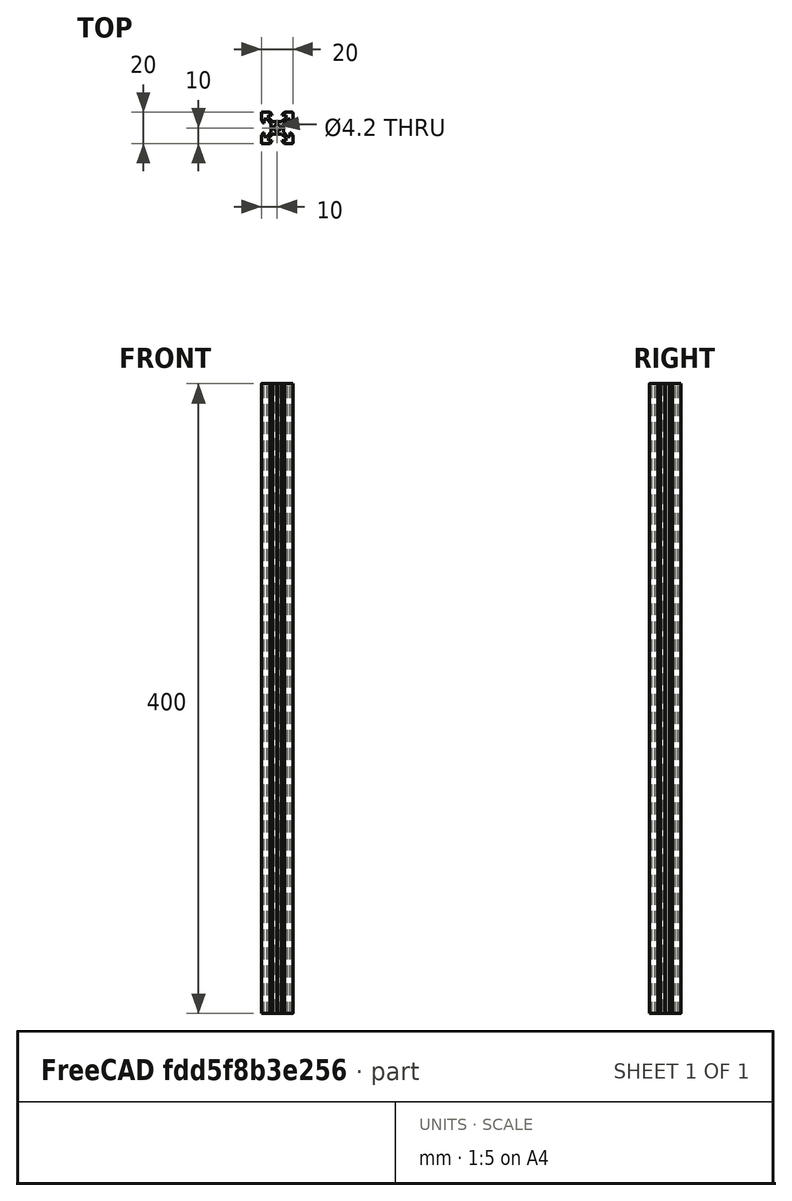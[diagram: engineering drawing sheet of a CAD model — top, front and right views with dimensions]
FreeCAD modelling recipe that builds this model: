
FCSTD DOCUMENT  (FreeCAD 0.19R)
Label: 2020-400
License: All rights reserved
LicenseURL: http://en.wikipedia.org/wiki/All_rights_reserved
objects: Sketcher::SketchObject×1, PartDesign::Pad×1, PartDesign::Body×1
note: 4 computed .brp shape members not serialized (recipe doc carries the construction recipe); baked Part::Feature solids carry a one-line shape summary decoded from their .brp

FEATURE [Sketcher::SketchObject] Sketch
  FullyConstrained = true
  MapMode = 5
  Support = -> [XY_Plane]
  sketch-geometry (65):
    g0: LineSegment StartX=-10 StartY=4.58 StartZ=0 EndX=-10 EndY=9.5 EndZ=0
    g1: LineSegment StartX=-9.5 StartY=10 StartZ=0 EndX=-4.58 EndY=10 EndZ=0
    g2: LineSegment StartX=-5.5 StartY=8.2 StartZ=0 EndX=-3.125 EndY=8.2 EndZ=0
    g3: LineSegment StartX=-8.2 StartY=5.5 StartZ=0 EndX=-8.2 EndY=3.125 EndZ=0
    g4: LineSegment StartX=-0.125 StartY=3.9 StartZ=0 EndX=-2.83934 EndY=3.9 EndZ=0
    g5: LineSegment StartX=-3.9 StartY=2.83934 StartZ=0 EndX=-3.9 EndY=0.125 EndZ=0
    g6: ArcOfCircle CenterX=0 CenterY=3.9 CenterZ=0 NormalX=0 NormalY=0 NormalZ=1 AngleXU=0 Radius=0.125 StartAngle=3.14159 EndAngle=6.28319
    g7: ArcOfCircle CenterX=-3.9 CenterY=0 CenterZ=0 NormalX=0 NormalY=0 NormalZ=1 AngleXU=0 Radius=0.125 StartAngle=4.71239 EndAngle=7.85398
    g8: ArcOfCircle CenterX=-9.5 CenterY=9.5 CenterZ=0 NormalX=0 NormalY=0 NormalZ=1 AngleXU=0 Radius=0.5 StartAngle=1.5708 EndAngle=3.14159
    g9: LineSegment StartX=-5.5 StartY=8.2 StartZ=0 EndX=-5.5 EndY=6.56066 EndZ=0
    g10: LineSegment StartX=-8.2 StartY=5.5 StartZ=0 EndX=-6.56066 EndY=5.5 EndZ=0
    g11: LineSegment StartX=-4.58 StartY=10 StartZ=0 EndX=-3.125 EndY=8.545 EndZ=0
    g12: LineSegment StartX=-3.125 StartY=8.545 StartZ=0 EndX=-3.125 EndY=8.2 EndZ=0
    g13: LineSegment StartX=-10 StartY=4.58 StartZ=0 EndX=-8.545 EndY=3.125 EndZ=0
    g14: LineSegment StartX=-8.545 StartY=3.125 StartZ=0 EndX=-8.2 EndY=3.125 EndZ=0
    g15: LineSegment StartX=-5.5 StartY=6.56066 StartZ=0 EndX=-2.83934 EndY=3.9 EndZ=0
    g16: LineSegment StartX=-6.56066 StartY=5.5 StartZ=0 EndX=-3.9 EndY=2.83934 EndZ=0
    g17: Circle CenterX=0 CenterY=0 CenterZ=0 NormalX=0 NormalY=0 NormalZ=1 AngleXU=0 Radius=2.1
    g18: LineSegment StartX=0.125 StartY=3.9 StartZ=0 EndX=2.83934 EndY=3.9 EndZ=0
    g19: LineSegment StartX=2.83934 StartY=3.9 StartZ=0 EndX=5.5 EndY=6.56066 EndZ=0
    g20: LineSegment StartX=5.5 StartY=6.56066 StartZ=0 EndX=5.5 EndY=8.2 EndZ=0
    g21: LineSegment StartX=3.125 StartY=8.2 StartZ=0 EndX=3.125 EndY=8.545 EndZ=0
    g22: LineSegment StartX=5.5 StartY=8.2 StartZ=0 EndX=3.125 EndY=8.2 EndZ=0
    g23: LineSegment StartX=4.58 StartY=10 StartZ=0 EndX=9.5 EndY=10 EndZ=0
    g24: ArcOfCircle CenterX=9.5 CenterY=9.5 CenterZ=0 NormalX=0 NormalY=0 NormalZ=1 AngleXU=0 Radius=0.5 StartAngle=1.9e-15 EndAngle=1.5708
    g25: LineSegment StartX=10 StartY=9.5 StartZ=0 EndX=10 EndY=4.58 EndZ=0
    g26: LineSegment StartX=10 StartY=4.58 StartZ=0 EndX=8.545 EndY=3.125 EndZ=0
    g27: LineSegment StartX=8.545 StartY=3.125 StartZ=0 EndX=8.2 EndY=3.125 EndZ=0
    g28: LineSegment StartX=8.2 StartY=3.125 StartZ=0 EndX=8.2 EndY=5.5 EndZ=0
    g29: LineSegment StartX=8.2 StartY=5.5 StartZ=0 EndX=6.56066 EndY=5.5 EndZ=0
    g30: LineSegment StartX=6.56066 StartY=5.5 StartZ=0 EndX=3.9 EndY=2.83934 EndZ=0
    g31: LineSegment StartX=3.9 StartY=2.83934 StartZ=0 EndX=3.9 EndY=0.125 EndZ=0
    g32: ArcOfCircle CenterX=3.9 CenterY=0 CenterZ=0 NormalX=0 NormalY=0 NormalZ=1 AngleXU=0 Radius=0.125 StartAngle=1.5708 EndAngle=4.71239
    g33: LineSegment StartX=3.9 StartY=-0.125 StartZ=0 EndX=3.9 EndY=-2.83934 EndZ=0
    g34: LineSegment StartX=3.9 StartY=-2.83934 StartZ=0 EndX=6.56066 EndY=-5.5 EndZ=0
    g35: LineSegment StartX=6.56066 StartY=-5.5 StartZ=0 EndX=8.2 EndY=-5.5 EndZ=0
    g36: LineSegment StartX=8.2 StartY=-5.5 StartZ=0 EndX=8.2 EndY=-3.125 EndZ=0
    g37: LineSegment StartX=8.2 StartY=-3.125 StartZ=0 EndX=8.545 EndY=-3.125 EndZ=0
    g38: LineSegment StartX=8.545 StartY=-3.125 StartZ=0 EndX=10 EndY=-4.58 EndZ=0
    g39: LineSegment StartX=10 StartY=-4.58 StartZ=0 EndX=10 EndY=-9.5 EndZ=0
    g40: ArcOfCircle CenterX=9.5 CenterY=-9.5 CenterZ=0 NormalX=0 NormalY=0 NormalZ=1 AngleXU=0 Radius=0.5 StartAngle=4.71239 EndAngle=6.28319
    g41: LineSegment StartX=9.5 StartY=-10 StartZ=0 EndX=4.58 EndY=-10 EndZ=0
    g42: LineSegment StartX=4.58 StartY=-10 StartZ=0 EndX=3.125 EndY=-8.545 EndZ=0
    g43: LineSegment StartX=2.83934 StartY=-3.9 StartZ=0 EndX=5.5 EndY=-6.56066 EndZ=0
    g44: LineSegment StartX=3.125 StartY=-8.545 StartZ=0 EndX=3.125 EndY=-8.2 EndZ=0
    g45: LineSegment StartX=3.125 StartY=-8.2 StartZ=0 EndX=5.5 EndY=-8.2 EndZ=0
    g46: LineSegment StartX=5.5 StartY=-8.2 StartZ=0 EndX=5.5 EndY=-6.56066 EndZ=0
    g47: ArcOfCircle CenterX=0 CenterY=-3.9 CenterZ=0 NormalX=0 NormalY=0 NormalZ=1 AngleXU=0 Radius=0.125 StartAngle=0 EndAngle=3.14159
    g48: LineSegment StartX=0.125 StartY=-3.9 StartZ=0 EndX=2.83934 EndY=-3.9 EndZ=0
    g49: LineSegment StartX=-0.125 StartY=-3.9 StartZ=0 EndX=-2.83934 EndY=-3.9 EndZ=0
    g50: LineSegment StartX=-3.9 StartY=-0.125 StartZ=0 EndX=-3.9 EndY=-2.83934 EndZ=0
    g51: LineSegment StartX=-3.9 StartY=-2.83934 StartZ=0 EndX=-6.56066 EndY=-5.5 EndZ=0
    g52: LineSegment StartX=-6.56066 StartY=-5.5 StartZ=0 EndX=-8.2 EndY=-5.5 EndZ=0
    g53: LineSegment StartX=-8.2 StartY=-5.5 StartZ=0 EndX=-8.2 EndY=-3.125 EndZ=0
    g54: LineSegment StartX=-8.2 StartY=-3.125 StartZ=0 EndX=-8.545 EndY=-3.125 EndZ=0
    g55: LineSegment StartX=-8.545 StartY=-3.125 StartZ=0 EndX=-10 EndY=-4.58 EndZ=0
    g56: LineSegment StartX=-10 StartY=-4.58 StartZ=0 EndX=-10 EndY=-9.5 EndZ=0
    g57: ArcOfCircle CenterX=-9.5 CenterY=-9.5 CenterZ=0 NormalX=0 NormalY=0 NormalZ=1 AngleXU=0 Radius=0.5 StartAngle=3.14159 EndAngle=4.71239
    g58: LineSegment StartX=-9.5 StartY=-10 StartZ=0 EndX=-4.58 EndY=-10 EndZ=0
    g59: LineSegment StartX=-4.58 StartY=-10 StartZ=0 EndX=-3.125 EndY=-8.545 EndZ=0
    g60: LineSegment StartX=-2.83934 StartY=-3.9 StartZ=0 EndX=-5.5 EndY=-6.56066 EndZ=0
    g61: LineSegment StartX=-5.5 StartY=-6.56066 StartZ=0 EndX=-5.5 EndY=-8.2 EndZ=0
    g62: LineSegment StartX=-5.5 StartY=-8.2 StartZ=0 EndX=-3.125 EndY=-8.2 EndZ=0
    g63: LineSegment StartX=-3.125 StartY=-8.545 StartZ=0 EndX=-3.125 EndY=-8.2 EndZ=0
    g64: LineSegment StartX=3.125 StartY=8.545 StartZ=0 EndX=4.58 EndY=10 EndZ=0
  constraints (194):
    c: Diameter(g17) = 4.2
    c: Radius(g32) = 0.125
    c: Coincident(g-1,g17)
    c: DistanceY(g57,g1) = 20
    c: DistanceX(g56,g39) = 20
    c: Radius(g57) = 0.5
    c: DistanceX(g56,g17) = 10
    c: DistanceY(g57,g17) = 10
    c: Distance(g5,g4) = 1.5
    c: DistanceY(g20,g23) = 1.8
    c: DistanceY(g18,g20) = 4.3
    c: DistanceX(g11,g21) = 6.25
    c: DistanceX(g1,g23) = 9.16
    c: DistanceX(g2,g20) = 11
    c: Coincident(g6,g18)
    c: Coincident(g6,g4)
    c: Coincident(g4,g15)
    c: Coincident(g18,g19)
    c: Coincident(g5,g16)
    c: Coincident(g16,g10)
    c: Coincident(g15,g9)
    c: Coincident(g12,g2)
    c: Coincident(g2,g9)
    c: Coincident(g12,g11)
    c: Coincident(g1,g11)
    c: Coincident(g23,g64)
    c: Coincident(g22,g21)
    c: Coincident(g64,g21)
    c: Coincident(g22,g20)
    c: Coincident(g19,g20)
    c: Coincident(g25,g26)
    c: Coincident(g27,g26)
    c: Coincident(g27,g28)
    c: Coincident(g28,g29)
    c: Coincident(g29,g30)
    c: Coincident(g0,g13)
    c: Coincident(g14,g13)
    c: Coincident(g14,g3)
    c: Coincident(g3,g10)
    c: Coincident(g5,g7)
    c: Coincident(g50,g7)
    c: Coincident(g51,g50)
    c: Coincident(g52,g51)
    c: Coincident(g52,g53)
    c: Coincident(g54,g53)
    c: Coincident(g55,g54)
    c: Coincident(g56,g55)
    c: Coincident(g58,g59)
    c: Coincident(g63,g59)
    c: Coincident(g62,g63)
    c: Coincident(g62,g61)
    c: Coincident(g60,g61)
    c: Coincident(g49,g60)
    c: Coincident(g47,g49)
    c: Coincident(g48,g47)
    c: Coincident(g48,g43)
    c: Coincident(g46,g43)
    c: Coincident(g45,g46)
    c: Coincident(g45,g44)
    c: Coincident(g42,g44)
    c: Coincident(g41,g42)
    c: Coincident(g39,g38)
    c: Coincident(g38,g37)
    c: Coincident(g37,g36)
    c: Coincident(g35,g36)
    c: Coincident(g34,g35)
    c: Coincident(g34,g33)
    c: Coincident(g31,g30)
    c: Coincident(g33,g32)
    c: Coincident(g32,g31)
    c: Vertical(g0)
    c: Horizontal(g1)
    c: Equal(g0,g1)
    c: Horizontal(g4)
    c: PointOnObject(g6,g-2)
    c: Horizontal(g18)
    c: Horizontal(g4,g6)
    c: Horizontal(g6,g6)
    c: Parallel(g13,g11)
    c: Horizontal(g14)
    c: Vertical(g12)
    c: Equal(g14,g12)
    c: Vertical(g3)
    c: Horizontal(g2)
    c: Equal(g3,g2)
    c: Equal(g10,g9)
    c: Horizontal(g10)
    c: Vertical(g9)
    c: Parallel(g16,g15)
    c: Equal(g13,g11)
    c: Tangent(g8,g0) = 1.5708
    c: PointOnObject(g7,g-1)
    c: Vertical(g5)
    c: Vertical(g50)
    c: Vertical(g7,g7)
    c: Vertical(g7,g5)
    c: Horizontal(g52)
    c: Vertical(g53)
    c: Horizontal(g54)
    c: Vertical(g56)
    c: Equal(g50,g5)
    c: Equal(g51,g16)
    c: Perpendicular(g16,g51)
    c: Equal(g52,g10)
    c: Equal(g53,g3)
    c: Equal(g54,g14)
    c: Equal(g55,g13)
    c: Perpendicular(g55,g13)
    c: Equal(g56,g0)
    c: Tangent(g57,g56) = -1.5708
    c: Tangent(g57,g58) = -1.5708
    c: Tangent(g8,g1) = 1.5708
    c: Equal(g57,g8)
    c: Horizontal(g58)
    c: Equal(g58,g56)
    c: Equal(g55,g59)
    c: Parallel(g55,g59)
    c: Vertical(g63)
    c: Equal(g63,g54)
    c: Horizontal(g62)
    c: Vertical(g61)
    c: Equal(g61,g52)
    c: Equal(g60,g51)
    c: Parallel(g60,g51)
    c: PointOnObject(g47,g-2)
    c: Horizontal(g47,g47)
    c: Horizontal(g47,g47)
    c: Horizontal(g49)
    c: Equal(g49,g50)
    c: Horizontal(g48)
    c: Vertical(g46)
    c: Perpendicular(g60,g43)
    c: Equal(g43,g60)
    c: Equal(g46,g61)
    c: Horizontal(g45)
    c: Equal(g45,g62)
    c: Vertical(g44)
    c: Equal(g44,g63)
    c: Perpendicular(g42,g59)
    c: Equal(g42,g59)
    c: Horizontal(g41)
    c: Equal(g58,g41)
    c: Tangent(g40,g41) = 1.5708
    c: Tangent(g40,g39) = 1.5708
    c: Equal(g57,g40)
    c: Vertical(g39)
    c: Equal(g41,g39)
    c: Parallel(g42,g38)
    c: Equal(g42,g38)
    c: Horizontal(g37)
    c: Equal(g44,g37)
    c: Vertical(g36)
    c: Equal(g45,g36)
    c: Horizontal(g35)
    c: Equal(g35,g46)
    c: Parallel(g43,g34)
    c: Equal(g43,g34)
    c: PointOnObject(g32,g-1)
    c: Vertical(g33)
    c: Vertical(g32,g31)
    c: Vertical(g31,g32)
    c: Equal(g48,g33)
    c: Equal(g47,g7)
    c: Equal(g7,g6)
    c: Vertical(g31)
    c: Equal(g33,g31)
    c: Equal(g4,g5)
    c: Equal(g4,g18)
    c: Parallel(g30,g19)
    c: Equal(g30,g19)
    c: Horizontal(g29)
    c: Vertical(g20)
    c: Equal(g35,g29)
    c: Equal(g29,g20)
    c: Horizontal(g22)
    c: Equal(g22,g2)
    c: Vertical(g21)
    c: Equal(g11,g64)
    c: Horizontal(g23)
    c: Equal(g1,g23)
    c: Vertical(g28)
    c: Equal(g28,g36)
    c: Horizontal(g27)
    c: Equal(g27,g37)
    c: Perpendicular(g38,g26)
    c: Equal(g38,g26)
    c: Vertical(g25)
    c: Equal(g39,g25)
    c: Tangent(g24,g23) = 1.5708
    c: Tangent(g24,g25) = 1.5708
    c: Vertical(g25,g38)
    c: Horizontal(g2,g21)
    c: Vertical(g10,g51)
    c: Angle(g64,g11) = 1.5708
FEATURE [PartDesign::Pad] Pad
  Direction = (1,1,1)
  Length = 400
  Length2 = 100
  Profile = -> Sketch
  Type = 0
FEATURE [PartDesign::Body] Body  label="2020-400"
  Group = -> [Sketch,Pad]
  Origin = -> Origin
  Tip = -> Pad
